# Revit family: 306_528cdc2072804c48a205e5b348d7bd
name_source: partatom
category: Pipe Accessories
revit_build: Autodesk Revit 2018 (Build: 20170223_1515(x64)
units: mm (PartAtom-declared; Revit-internal decimal feet)

## family parameters
Always vertical = Yes
Cut with Voids When Loaded = No
Part Type = Valve - Breaks Into
Round Connector Dimension = Use Diameter
Shared = No
Work Plane-Based = No

## types (3) — shared parameters
CAT0 = Yes
Description = Pressure Reducing Valve with flange connection
L2D_Min = 3048 mm
Manufacturer = SYR
QmdConnectorList = 301;D;302;D
magiPartTypeId = 306
magiProductFamilyId = 528cdc2072804c48a205e5b348d7bd

## per-type parameters (varying)
| type | CenSd_SW1_6 | CenSd_SW2_6 | D | D2 | D4 | D5 | D6 | D7 | H11 | H12 | H2 | H4 | H8 | H9 | L1 | L2 | L2D | L3 | L5 | SW1 | SW2 | W2D | magiProductId |
| SYR-6247-100 | 13 mm | 36 mm | 100 mm | 12 mm  [stored 0.0393701 ft] | 36 mm | 28 mm | 25 mm  [stored 0.082021 ft] | 22 mm  [stored 0.0721785 ft] | 130 mm | 38 mm | 110 mm  [stored 0.360892 ft] | 44 mm  [stored 0.144357 ft] | 68 mm | 102 mm  [stored 0.334646 ft] | 175 mm | 29 mm | 350 mm | 15 mm  [stored 0.0492126 ft] | 292 mm | 15 mm  [stored 0.0492126 ft] | 41 mm | 100 mm  [stored 0.328084 ft] | 750dd84a4a7e44ed922dc4e65ed96b |
| SYR-6247-80 | 11 mm | 32 mm | 80 mm | 10 mm  [stored 0.0328084 ft] | 33 mm | 25 mm  [stored 0.082021 ft] | 23 mm | 20 mm | 137 mm | 41 mm | 100 mm  [stored 0.328084 ft] | 40 mm | 62 mm | 92 mm | 155 mm | 26 mm | 310 mm | 13 mm | 258 mm | 13 mm | 38 mm | 80 mm | 01e9e86bc7b94ee0b3dcf4748fb42f |
| SYR-6247-65 | 10 mm  [stored 0.0328084 ft] | 30 mm  [stored 0.0984252 ft] | 65 mm | 10 mm  [stored 0.0328084 ft] | 30 mm  [stored 0.0984252 ft] | 23 mm | 21 mm | 19 mm | 143 mm | 43 mm | 93 mm | 37 mm | 57 mm | 85 mm | 145 mm | 24 mm | 290 mm | 12 mm  [stored 0.0393701 ft] | 242 mm | 12 mm  [stored 0.0393701 ft] | 35 mm | 65 mm | a93919ad1ebb42ceabda909ef8034b |

note: column(s) folded — value = type name in every type: MC Product Code

note: [stored X ft] marks values corroborated as IEEE doubles in the binary element streams (Revit-internal decimal feet)

## geometry (parser evidence)
native form markers: Sweep x1
no freeform markers — native parametric forms only
